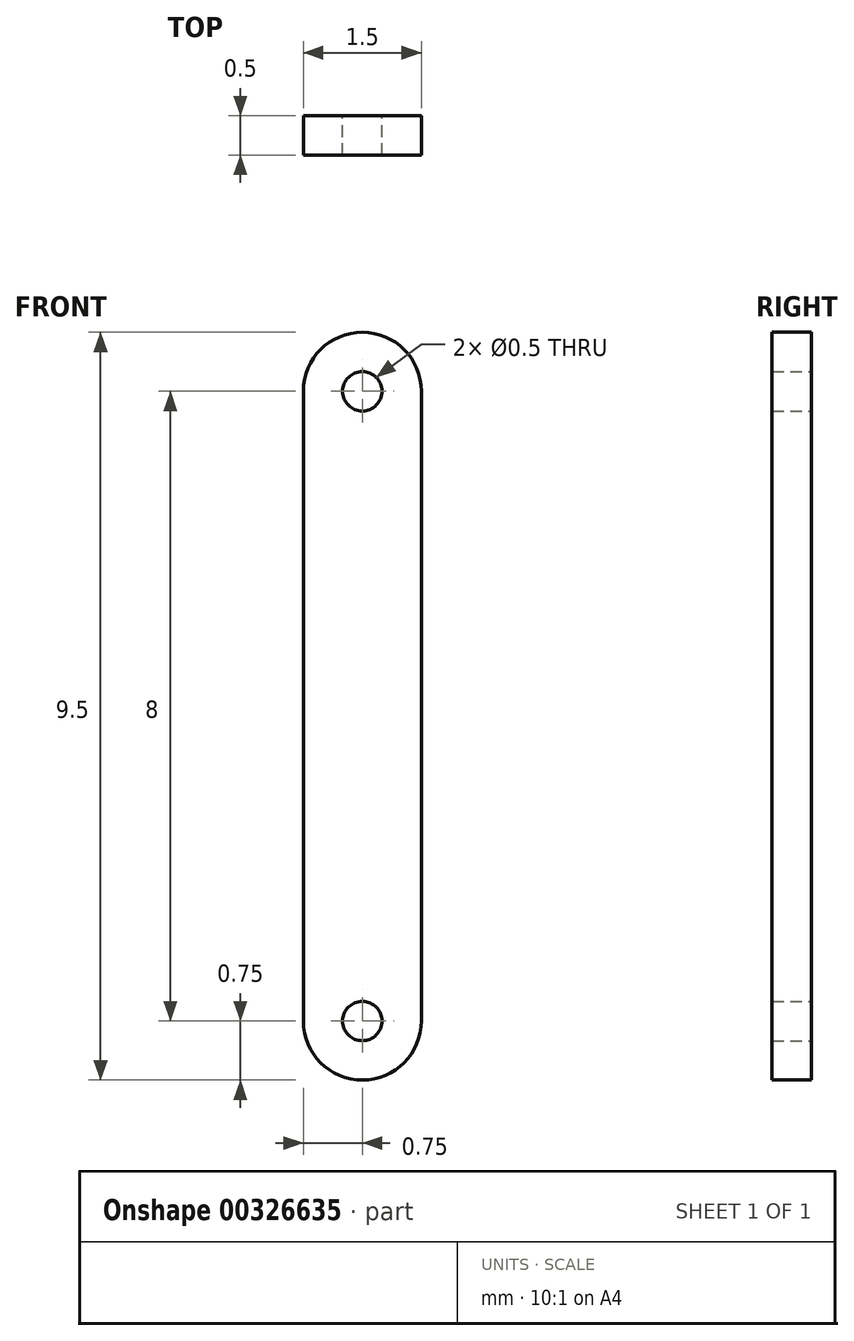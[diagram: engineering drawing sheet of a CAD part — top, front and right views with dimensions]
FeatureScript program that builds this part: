
annotation { "Feature Type Name" : "Feature", "Feature Type Description" : "" }
export const myFeature = defineFeature(function(context is Context, id is Id, definition is map)
    precondition{}
    {
        {
            var Q0;
            Q0=qCreatedBy(makeId("Front.planeOp"),FACE);
            var sketch = newSketch(context, id + "F0", { "sketchPlane" : qUnion([Q0])});
            skLineSegment(sketch, "E0.bottom", {"start": v(0, -4.75) * mm, "end": v(0, -4.75) * mm});
            skLineSegment(sketch, "E0.top", {"start": v(0, 4.75) * mm, "end": v(0, 4.75) * mm});
            skLineSegment(sketch, "E0.left", {"start": v(0.75, -4) * mm, "end": v(0.75, 4) * mm});
            skLineSegment(sketch, "E0.right", {"start": v(-0.75, -4) * mm, "end": v(-0.75, 4) * mm});
            skPoint(sketch, "E0.middle", {"position": v(0, 0) * mm});
            skArc(sketch, "E1.filletArc", {"start": v(0.75, 4) * mm, "mid": v(0.53, 4.53) * mm, "end": v(0, 4.75) * mm});
            skArc(sketch, "E2.filletArc", {"start": v(0, 4.75) * mm, "mid": v(-0.53, 4.53) * mm, "end": v(-0.75, 4) * mm});
            skArc(sketch, "E3.filletArc", {"start": v(-0.75, -4) * mm, "mid": v(-0.53, -4.53) * mm, "end": v(0, -4.75) * mm});
            skArc(sketch, "E4.filletArc", {"start": v(0, -4.75) * mm, "mid": v(0.53, -4.53) * mm, "end": v(0.75, -4) * mm});
            skCircle(sketch, "E5", {"center": v(0, 4) * mm, "radius": 0.25 * mm});
            skCircle(sketch, "E6", {"center": v(0, -4) * mm, "radius": 0.25 * mm});
            skSolve(sketch);
        }
        {
            var Q0;
            Q0=makeQuery(id+"F0.imprint","IMPRINT",FACE,{"disambiguationData":[TD([[makeQuery(id+"F0.imprint","IMPRINT",EDGE,{"derivedFrom":sQuery(id+"F0.wireOp",EDGE,"E0.left")}),1.0]])]});
            extrude(context, id + "F1", {"entities" : qUnion([Q0]), "depth" : 0.5 * mm});
        }
    });
